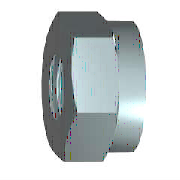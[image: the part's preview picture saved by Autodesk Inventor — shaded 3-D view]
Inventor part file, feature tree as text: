
AUTODESK INVENTOR PART (.ipt)
format: ipt  version: 2024 (Build 280153000, 153)  size: 178,176 bytes
history: native  units: mm (DEFAULTED — no unit token found)
features: extrude x2, other x2, hole x1, plane x1
ambient origin geometry x7: Origin, YZ Plane, XZ Plane, X Axis, Y Axis, Z Axis, Center Point
bodies: Solid1 (feature_tree)
feature tree (6):
  extrude  "Базовый элемент"  Depth=9.237604mm
  extrude  "Кольцо"  Depth=3.2mm
  other  "Фаска1"
  hole  "Резьба"  [1 undecoded]
  other  "Work Axis1"
  plane  "Work Plane1"
note: 1 required parameter value undecoded (feature->parameter linkage not recoverable at this tier; creation-order binding heuristic only, values carry confidence <= 0.55)
